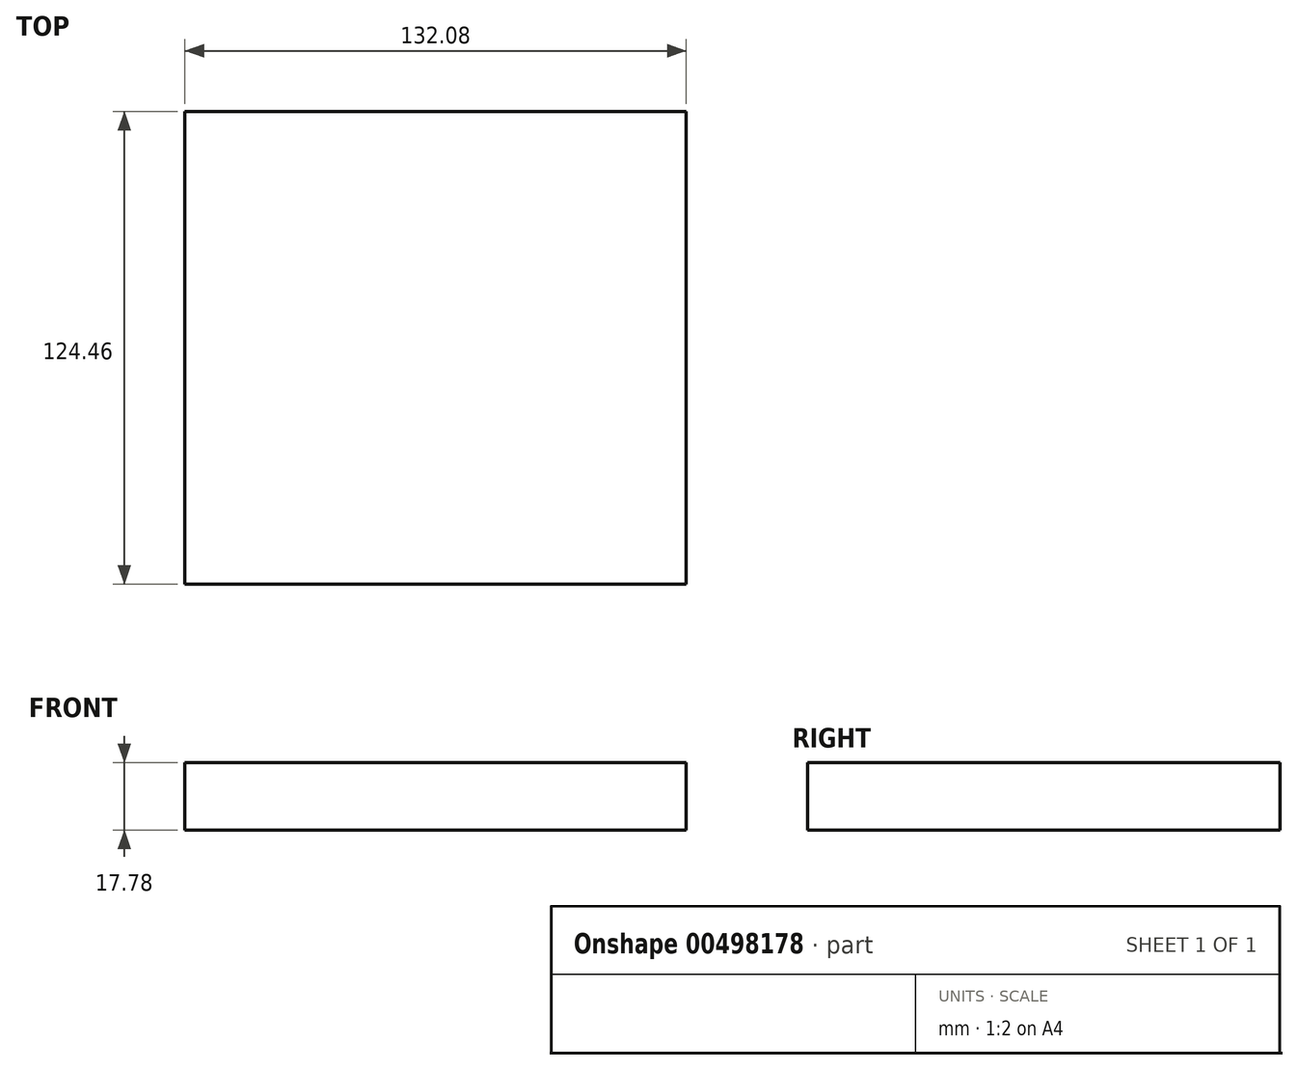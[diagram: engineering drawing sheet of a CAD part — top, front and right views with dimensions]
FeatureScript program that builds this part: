
annotation { "Feature Type Name" : "Feature", "Feature Type Description" : "" }
export const myFeature = defineFeature(function(context is Context, id is Id, definition is map)
    precondition{}
    {
        {
            var Q0;
            Q0=qCreatedBy(makeId("Top.planeOp"),FACE);
            var sketch = newSketch(context, id + "F0", { "sketchPlane" : qUnion([Q0])});
            skLineSegment(sketch, "E0.bottom", {"start": v(66.04, 62.23) * mm, "end": v(-66.04, 62.23) * mm});
            skLineSegment(sketch, "E0.top", {"start": v(66.04, -62.23) * mm, "end": v(-66.04, -62.23) * mm});
            skLineSegment(sketch, "E0.left", {"start": v(66.04, 62.23) * mm, "end": v(66.04, -62.23) * mm});
            skLineSegment(sketch, "E0.right", {"start": v(-66.04, 62.23) * mm, "end": v(-66.04, -62.23) * mm});
            skPoint(sketch, "E0.middle", {"position": v(0, 0) * mm});
            skSolve(sketch);
        }
        {
            var Q0;
            Q0 = qSketchRegion(id + "F0", true);
            extrude(context, id + "F1", {"entities" : qUnion([Q0]), "depth" : 17.78 * mm});
        }
    });
